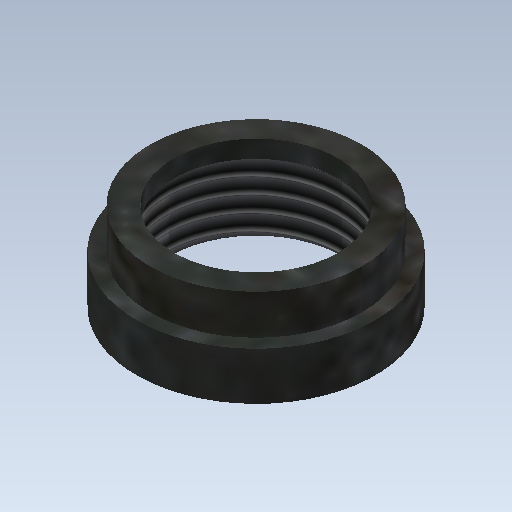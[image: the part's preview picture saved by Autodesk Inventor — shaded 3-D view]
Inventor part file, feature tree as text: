
AUTODESK INVENTOR PART (.ipt)
format: ipt  version: 2020 (Build 240168000, 168)  size: 180,736 bytes
history: native  units: mm
features: extrude x3, sketch x3, hole x1
ambient origin geometry x8: Origin, YZ Plane, XZ Plane, XY Plane, X Axis, Y Axis, Z Axis, Center Point
bodies: Solid1 (feature_tree)
feature tree (7):
  extrude  "Extrusion1"  Depth=3.0mm TaperAngle=0.0deg
  extrude  "Extrusion2"  Depth=2.5mm TaperAngle=0.0deg
  extrude  "Extrusion3"  Depth=2.5mm TaperAngle=0.0deg
  hole  "Hole1"  [1 undecoded]
  sketch  "Sketch1"  dims[d0=15.0mm d1=3.0mm d2=0.0mm]
  sketch  "Sketch2"  dims[d3=13.3mm d4=2.5mm d5=0.0mm]
  sketch  "Sketch3"  dims[d6=10.3mm d7=2.5mm d8=0.0mm d18=10.0mm d19=10.0mm d11=10.917mm d12=24.0mm d13=4.0mm d14=2.0mm d15=90.0deg d16=4.4mm d17=0.0mm]
note: 1 required parameter value undecoded (feature->parameter linkage not recoverable at this tier; creation-order binding heuristic only, values carry confidence <= 0.55)
